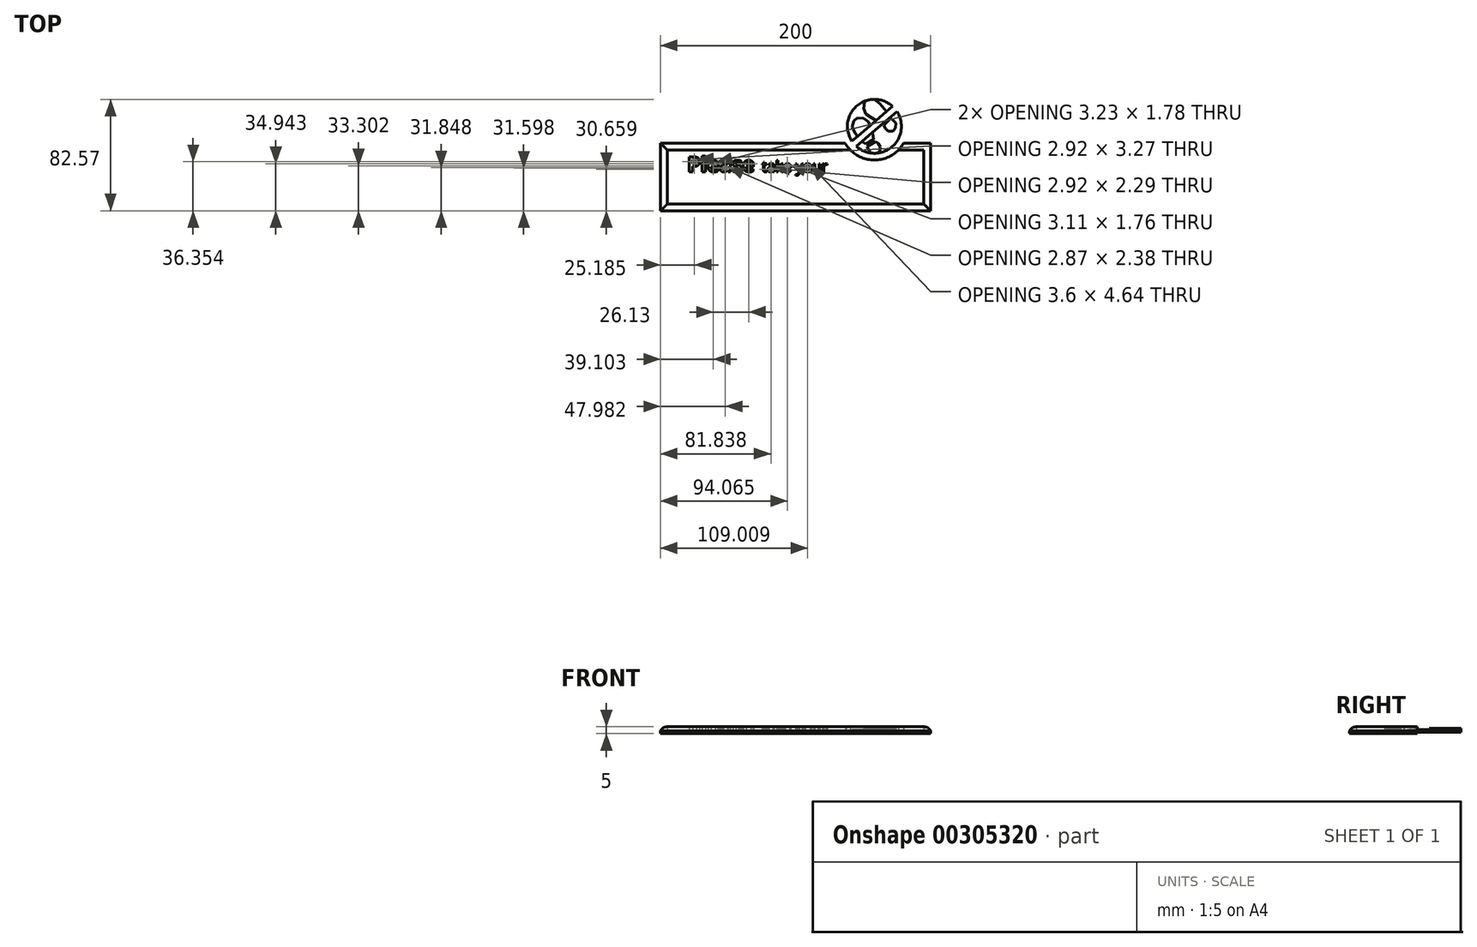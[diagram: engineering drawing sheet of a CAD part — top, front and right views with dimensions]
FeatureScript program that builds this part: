
annotation { "Feature Type Name" : "Feature", "Feature Type Description" : "" }
export const myFeature = defineFeature(function(context is Context, id is Id, definition is map)
    precondition{}
    {
        {
            var Q0;
            Q0=qCreatedBy(makeId("Top.planeOp"),FACE);
            var sketch = newSketch(context, id + "F0", { "sketchPlane" : qUnion([Q0])});
            skLineSegment(sketch, "E0.top", {"start": v(-121.35, -25.22) * mm, "end": v(78.65, -25.22) * mm});
            skLineSegment(sketch, "E0.left", {"start": v(-121.35, 24.78) * mm, "end": v(-121.35, -25.22) * mm});
            skLineSegment(sketch, "E0.right", {"start": v(78.65, 24.78) * mm, "end": v(78.65, -25.22) * mm});
            skCircle(sketch, "E1", {"center": v(37.04, 37.35) * mm, "radius": 25 * mm});
            skPoint(sketch, "E1.first.point", {"position": v(15.44, 24.78) * mm});
            skCircle(sketch, "E2", {"center": v(37.04, 37.35) * mm, "radius": 20 * mm});
            skLineSegment(sketch, "E3", {"start": v(20.32, 26.39) * mm, "end": v(50.53, 52.12) * mm});
            skLineSegment(sketch, "E4", {"start": v(53.77, 48.31) * mm, "end": v(23.56, 22.58) * mm});
            skLineSegment(sketch, "E5", {"start": v(20.32, 26.39) * mm, "end": v(23.56, 22.58) * mm, "construction": true});
            skLineSegment(sketch, "E6", {"start": v(21.94, 24.48) * mm, "end": v(52.27, 50.32) * mm, "construction": true});
            skPoint(sketch, "E7", {"position": v(58.65, 24.78) * mm});
            skLineSegment(sketch, "E8", {"start": v(-121.35, 24.78) * mm, "end": v(15.44, 24.78) * mm});
            skLineSegment(sketch, "E9", {"start": v(58.65, 24.78) * mm, "end": v(78.65, 24.78) * mm});
            skLineSegment(sketch, "E10", {"start": v(30.68, 24.1) * mm, "end": v(36.58, 27.82) * mm});
            skLineSegment(sketch, "E11", {"start": v(36.58, 27.82) * mm, "end": v(35.77, 32.31) * mm});
            skLineSegment(sketch, "E12", {"start": v(34.65, 36) * mm, "end": v(32.57, 40.8) * mm});
            skLineSegment(sketch, "E13", {"start": v(32.57, 40.8) * mm, "end": v(29.04, 43.21) * mm});
            skLineSegment(sketch, "E14", {"start": v(29.04, 43.21) * mm, "end": v(24.28, 43.73) * mm});
            skLineSegment(sketch, "E15", {"start": v(24.28, 43.73) * mm, "end": v(21.68, 41.4) * mm});
            skLineSegment(sketch, "E16", {"start": v(21.68, 41.4) * mm, "end": v(20.64, 36.9) * mm});
            skLineSegment(sketch, "E17", {"start": v(20.64, 36.9) * mm, "end": v(22.8, 32.31) * mm});
            skLineSegment(sketch, "E18", {"start": v(22.8, 32.31) * mm, "end": v(27.74, 26.17) * mm});
            skLineSegment(sketch, "E19", {"start": v(27.74, 26.17) * mm, "end": v(30.68, 24.1) * mm});
            skLineSegment(sketch, "E20", {"start": v(31.8, 22.28) * mm, "end": v(37.95, 26.17) * mm});
            skLineSegment(sketch, "E21", {"start": v(37.95, 26.17) * mm, "end": v(39.94, 24.61) * mm});
            skLineSegment(sketch, "E22", {"start": v(39.94, 24.61) * mm, "end": v(41.5, 22.02) * mm});
            skLineSegment(sketch, "E23", {"start": v(41.5, 22.02) * mm, "end": v(40.72, 18.47) * mm});
            skLineSegment(sketch, "E24", {"start": v(40.72, 18.47) * mm, "end": v(38.2, 17.09) * mm});
            skLineSegment(sketch, "E25", {"start": v(38.2, 17.09) * mm, "end": v(34.23, 17.78) * mm});
            skLineSegment(sketch, "E26", {"start": v(34.23, 17.78) * mm, "end": v(32.76, 20.03) * mm});
            skLineSegment(sketch, "E27", {"start": v(32.76, 20.03) * mm, "end": v(31.8, 22.28) * mm});
            skLineSegment(sketch, "E28", {"start": v(34.65, 36) * mm, "end": v(35.77, 32.31) * mm});
            skLineSegment(sketch, "E29", {"start": v(25.33, 53.56) * mm, "end": v(50.32, 22.39) * mm, "construction": true});
            skLineSegment(sketch, "E30.MirrorCS", {"start": v(29.21, 50.51) * mm, "end": v(29.74, 55.27) * mm});
            skLineSegment(sketch, "E31.MirrorCS", {"start": v(29.74, 55.27) * mm, "end": v(32.59, 57.3) * mm});
            skLineSegment(sketch, "E32.MirrorCS", {"start": v(32.59, 57.3) * mm, "end": v(37.2, 57.33) * mm});
            skLineSegment(sketch, "E33.MirrorCS", {"start": v(37.2, 57.33) * mm, "end": v(41.2, 54.22) * mm});
            skLineSegment(sketch, "E34.MirrorCS", {"start": v(41.2, 54.22) * mm, "end": v(46.13, 48.07) * mm});
            skLineSegment(sketch, "E35.MirrorCS", {"start": v(46.13, 48.07) * mm, "end": v(47.52, 44.75) * mm});
            skLineSegment(sketch, "E36.MirrorCS", {"start": v(47.52, 44.75) * mm, "end": v(42.6, 39.8) * mm});
            skLineSegment(sketch, "E37.MirrorCS", {"start": v(42.6, 39.8) * mm, "end": v(38.39, 41.56) * mm});
            skLineSegment(sketch, "E38.MirrorCS", {"start": v(35.03, 43.46) * mm, "end": v(38.39, 41.56) * mm});
            skLineSegment(sketch, "E39.MirrorCS", {"start": v(35.03, 43.46) * mm, "end": v(30.8, 46.54) * mm});
            skLineSegment(sketch, "E40.MirrorCS", {"start": v(30.8, 46.54) * mm, "end": v(29.21, 50.51) * mm});
            skLineSegment(sketch, "E41.MirrorCS", {"start": v(49.05, 43.26) * mm, "end": v(43.9, 38.1) * mm});
            skLineSegment(sketch, "E42.MirrorCS", {"start": v(43.9, 38.1) * mm, "end": v(45, 35.83) * mm});
            skLineSegment(sketch, "E43.MirrorCS", {"start": v(45, 35.83) * mm, "end": v(47.2, 33.74) * mm});
            skLineSegment(sketch, "E44.MirrorCS", {"start": v(47.2, 33.74) * mm, "end": v(50.82, 33.73) * mm});
            skLineSegment(sketch, "E45.MirrorCS", {"start": v(50.82, 33.73) * mm, "end": v(52.72, 35.88) * mm});
            skLineSegment(sketch, "E46.MirrorCS", {"start": v(52.72, 35.88) * mm, "end": v(52.9, 39.91) * mm});
            skLineSegment(sketch, "E47.MirrorCS", {"start": v(52.9, 39.91) * mm, "end": v(51.03, 41.84) * mm});
            skLineSegment(sketch, "E48.MirrorCS", {"start": v(51.03, 41.84) * mm, "end": v(49.05, 43.26) * mm});
            skText(sketch, "E49", { "text": "Please", "fontName": "OpenSans-Bold.ttf"});
            skText(sketch, "E50", { "text": "take your", "fontName": "OpenSans-Regular.ttf"});
            skText(sketch, "E51", { "text": "shoes off!", "fontName": "OpenSans-Bold.ttf"});
            skLineSegment(sketch, "E52.0", {"start": v(-116.35, 19.78) * mm, "end": v(19.27, 19.78) * mm});
            skLineSegment(sketch, "E52.1", {"start": v(54.82, 19.78) * mm, "end": v(73.65, 19.78) * mm});
            skLineSegment(sketch, "E52.2", {"start": v(73.65, 19.78) * mm, "end": v(73.65, -20.22) * mm});
            skLineSegment(sketch, "E52.3", {"start": v(-116.35, -20.22) * mm, "end": v(73.65, -20.22) * mm});
            skLineSegment(sketch, "E52.4", {"start": v(-116.35, 19.78) * mm, "end": v(-116.35, -20.22) * mm});
            skLineSegment(sketch, "E53", {"start": v(37.04, 37.35) * mm, "end": v(37.04, 62.35) * mm, "construction": true});
            const initialGuessF0  = {"E49": [-0.10135, 0.00366, 1, 0, 0.01112], "E50": [-0.04635, 0.00366, 1, 0, 0.008], "E51": [-0.03483, -0.01522, 1, 0, 0.014]};
            skSetInitialGuess(sketch, initialGuessF0);
            skSolve(sketch);
        }
        {
            var Q0;
            Q0=makeQuery(id+"F0.imprint","IMPRINT",FACE,{"disambiguationData":[TD([[makeQuery(id+"F0.imprint","IMPRINT",EDGE,{"derivedFrom":sQuery(id+"F0.wireOp",EDGE,"E0.top")}),1.0]])]});
            var Q1;
            Q1=makeQuery(id+"F0.imprint","IMPRINT",FACE,{"disambiguationData":[TD([[makeQuery(id+"F0.imprint","IMPRINT",EDGE,{"derivedFrom":sQuery(id+"F0.wireOp",EDGE,"E49.sketch_text.stroke-7")}),1.0]])]});
            var Q2;
            Q2=makeQuery(id+"F0.imprint","IMPRINT",FACE,{"disambiguationData":[TD([[makeQuery(id+"F0.imprint","IMPRINT",EDGE,{"derivedFrom":sQuery(id+"F0.wireOp",EDGE,"E49.sketch_text.stroke-0")}),1.0]])]});
            var Q3;
            Q3=makeQuery(id+"F0.imprint","IMPRINT",FACE,{"disambiguationData":[TD([[makeQuery(id+"F0.imprint","IMPRINT",EDGE,{"derivedFrom":sQuery(id+"F0.wireOp",EDGE,"E49.sketch_text.stroke-20")}),1.0]])]});
            var Q4;
            Q4=makeQuery(id+"F0.imprint","IMPRINT",FACE,{"disambiguationData":[TD([[makeQuery(id+"F0.imprint","IMPRINT",EDGE,{"derivedFrom":sQuery(id+"F0.wireOp",EDGE,"E49.sketch_text.stroke-58")}),1.0]])]});
            var Q5;
            Q5=makeQuery(id+"F0.imprint","IMPRINT",FACE,{"disambiguationData":[TD([[makeQuery(id+"F0.imprint","IMPRINT",EDGE,{"derivedFrom":sQuery(id+"F0.wireOp",EDGE,"E49.sketch_text.stroke-91")}),1.0]])]});
            var Q6;
            Q6=makeQuery(id+"F0.imprint","IMPRINT",FACE,{"disambiguationData":[TD([[makeQuery(id+"F0.imprint","IMPRINT",EDGE,{"derivedFrom":sQuery(id+"F0.wireOp",EDGE,"E50.sketch_text.stroke-38")}),1.0]])]});
            var Q7;
            Q7=makeQuery(id+"F0.imprint","IMPRINT",FACE,{"disambiguationData":[TD([[makeQuery(id+"F0.imprint","IMPRINT",EDGE,{"derivedFrom":sQuery(id+"F0.wireOp",EDGE,"E50.sketch_text.stroke-75")}),1.0]])]});
            var Q8;
            Q8=makeQuery(id+"F0.imprint","IMPRINT",FACE,{"disambiguationData":[TD([[makeQuery(id+"F0.imprint","IMPRINT",EDGE,{"derivedFrom":sQuery(id+"F0.wireOp",EDGE,"E50.sketch_text.stroke-105")}),1.0]])]});
            var Q9;
            Q9=makeQuery(id+"F0.imprint","IMPRINT",FACE,{"disambiguationData":[TD([[makeQuery(id+"F0.imprint","IMPRINT",EDGE,{"derivedFrom":sQuery(id+"F0.wireOp",EDGE,"E51.sketch_text.stroke-0")}),-1.0]])]});
            var Q10;
            Q10=makeQuery(id+"F0.imprint","IMPRINT",FACE,{"disambiguationData":[TD([[makeQuery(id+"F0.imprint","IMPRINT",EDGE,{"derivedFrom":sQuery(id+"F0.wireOp",EDGE,"E51.sketch_text.stroke-26")}),-1.0]])]});
            var Q11;
            Q11=makeQuery(id+"F0.imprint","IMPRINT",FACE,{"disambiguationData":[TD([[makeQuery(id+"F0.imprint","IMPRINT",EDGE,{"derivedFrom":sQuery(id+"F0.wireOp",EDGE,"E51.sketch_text.stroke-43")}),-1.0]])]});
            var Q12;
            Q12=makeQuery(id+"F0.imprint","IMPRINT",FACE,{"disambiguationData":[TD([[makeQuery(id+"F0.imprint","IMPRINT",EDGE,{"derivedFrom":sQuery(id+"F0.wireOp",EDGE,"E51.sketch_text.stroke-43")}),1.0]])]});
            var Q13;
            Q13=makeQuery(id+"F0.imprint","IMPRINT",FACE,{"disambiguationData":[TD([[makeQuery(id+"F0.imprint","IMPRINT",EDGE,{"derivedFrom":sQuery(id+"F0.wireOp",EDGE,"E51.sketch_text.stroke-61")}),1.0]])]});
            var Q14;
            Q14=makeQuery(id+"F0.imprint","IMPRINT",FACE,{"disambiguationData":[TD([[makeQuery(id+"F0.imprint","IMPRINT",EDGE,{"derivedFrom":sQuery(id+"F0.wireOp",EDGE,"E51.sketch_text.stroke-61")}),-1.0]])]});
            var Q15;
            Q15=makeQuery(id+"F0.imprint","IMPRINT",FACE,{"disambiguationData":[TD([[makeQuery(id+"F0.imprint","IMPRINT",EDGE,{"derivedFrom":sQuery(id+"F0.wireOp",EDGE,"E51.sketch_text.stroke-81")}),-1.0]])]});
            var Q16;
            Q16=makeQuery(id+"F0.imprint","IMPRINT",FACE,{"disambiguationData":[TD([[makeQuery(id+"F0.imprint","IMPRINT",EDGE,{"derivedFrom":sQuery(id+"F0.wireOp",EDGE,"E51.sketch_text.stroke-107")}),-1.0]])]});
            var Q17;
            Q17=makeQuery(id+"F0.imprint","IMPRINT",FACE,{"disambiguationData":[TD([[makeQuery(id+"F0.imprint","IMPRINT",EDGE,{"derivedFrom":sQuery(id+"F0.wireOp",EDGE,"E51.sketch_text.stroke-107")}),1.0]])]});
            var Q18;
            Q18=makeQuery(id+"F0.imprint","IMPRINT",FACE,{"disambiguationData":[TD([[makeQuery(id+"F0.imprint","IMPRINT",EDGE,{"derivedFrom":sQuery(id+"F0.wireOp",EDGE,"E51.sketch_text.stroke-143")}),-1.0]])]});
            var Q19;
            Q19=makeQuery(id+"F0.imprint","IMPRINT",FACE,{"disambiguationData":[TD([[makeQuery(id+"F0.imprint","IMPRINT",EDGE,{"derivedFrom":sQuery(id+"F0.wireOp",EDGE,"E51.sketch_text.stroke-161")}),-1.0]])]});
            var Q20;
            Q20=makeQuery(id+"F0.imprint","IMPRINT",FACE,{"disambiguationData":[TD([[makeQuery(id+"F0.imprint","IMPRINT",EDGE,{"derivedFrom":sQuery(id+"F0.wireOp",EDGE,"E51.sketch_text.stroke-165")}),-1.0]])]});
            var Q21;
            Q21=makeQuery(id+"F0.imprint","IMPRINT",FACE,{"disambiguationData":[TD([[makeQuery(id+"F0.imprint","IMPRINT",EDGE,{"derivedFrom":sQuery(id+"F0.wireOp",EDGE,"E51.sketch_text.stroke-125")}),-1.0]])]});
            var Q22;
            Q22=makeQuery(id+"F0.imprint","IMPRINT",FACE,{"disambiguationData":[TD([[makeQuery(id+"F0.imprint","IMPRINT",EDGE,{"derivedFrom":sQuery(id+"F0.wireOp",EDGE,"E49.sketch_text.stroke-0")}),-1.0]])]});
            var Q23;
            Q23=makeQuery(id+"F0.imprint","IMPRINT",FACE,{"disambiguationData":[TD([[makeQuery(id+"F0.imprint","IMPRINT",EDGE,{"derivedFrom":sQuery(id+"F0.wireOp",EDGE,"E49.sketch_text.stroke-16")}),-1.0]])]});
            var Q24;
            Q24=makeQuery(id+"F0.imprint","IMPRINT",FACE,{"disambiguationData":[TD([[makeQuery(id+"F0.imprint","IMPRINT",EDGE,{"derivedFrom":sQuery(id+"F0.wireOp",EDGE,"E49.sketch_text.stroke-20")}),-1.0]])]});
            var Q25;
            Q25=makeQuery(id+"F0.imprint","IMPRINT",FACE,{"disambiguationData":[TD([[makeQuery(id+"F0.imprint","IMPRINT",EDGE,{"derivedFrom":sQuery(id+"F0.wireOp",EDGE,"E49.sketch_text.stroke-40")}),-1.0]])]});
            var Q26;
            Q26=makeQuery(id+"F0.imprint","IMPRINT",FACE,{"disambiguationData":[TD([[makeQuery(id+"F0.imprint","IMPRINT",EDGE,{"derivedFrom":sQuery(id+"F0.wireOp",EDGE,"E49.sketch_text.stroke-65")}),-1.0]])]});
            var Q27;
            Q27=makeQuery(id+"F0.imprint","IMPRINT",FACE,{"disambiguationData":[TD([[makeQuery(id+"F0.imprint","IMPRINT",EDGE,{"derivedFrom":sQuery(id+"F0.wireOp",EDGE,"E49.sketch_text.stroke-91")}),-1.0]])]});
            var Q28;
            Q28=makeQuery(id+"F0.imprint","IMPRINT",FACE,{"disambiguationData":[TD([[makeQuery(id+"F0.imprint","IMPRINT",EDGE,{"derivedFrom":sQuery(id+"F0.wireOp",EDGE,"E50.sketch_text.stroke-0")}),-1.0]])]});
            var Q29;
            Q29=makeQuery(id+"F0.imprint","IMPRINT",FACE,{"disambiguationData":[TD([[makeQuery(id+"F0.imprint","IMPRINT",EDGE,{"derivedFrom":sQuery(id+"F0.wireOp",EDGE,"E50.sketch_text.stroke-19")}),-1.0]])]});
            var Q30;
            Q30=makeQuery(id+"F0.imprint","IMPRINT",FACE,{"disambiguationData":[TD([[makeQuery(id+"F0.imprint","IMPRINT",EDGE,{"derivedFrom":sQuery(id+"F0.wireOp",EDGE,"E50.sketch_text.stroke-46")}),-1.0]])]});
            var Q31;
            Q31=makeQuery(id+"F0.imprint","IMPRINT",FACE,{"disambiguationData":[TD([[makeQuery(id+"F0.imprint","IMPRINT",EDGE,{"derivedFrom":sQuery(id+"F0.wireOp",EDGE,"E50.sketch_text.stroke-61")}),-1.0]])]});
            var Q32;
            Q32=makeQuery(id+"F0.imprint","IMPRINT",FACE,{"disambiguationData":[TD([[makeQuery(id+"F0.imprint","IMPRINT",EDGE,{"derivedFrom":sQuery(id+"F0.wireOp",EDGE,"E50.sketch_text.stroke-80")}),-1.0]])]});
            var Q33;
            Q33=makeQuery(id+"F0.imprint","IMPRINT",FACE,{"disambiguationData":[TD([[makeQuery(id+"F0.imprint","IMPRINT",EDGE,{"derivedFrom":sQuery(id+"F0.wireOp",EDGE,"E50.sketch_text.stroke-96")}),-1.0]])]});
            var Q34;
            Q34=makeQuery(id+"F0.imprint","IMPRINT",FACE,{"disambiguationData":[TD([[makeQuery(id+"F0.imprint","IMPRINT",EDGE,{"derivedFrom":sQuery(id+"F0.wireOp",EDGE,"E50.sketch_text.stroke-113")}),-1.0]])]});
            var Q35;
            Q35=makeQuery(id+"F0.imprint","IMPRINT",FACE,{"disambiguationData":[TD([[makeQuery(id+"F0.imprint","IMPRINT",EDGE,{"derivedFrom":sQuery(id+"F0.wireOp",EDGE,"E50.sketch_text.stroke-130")}),-1.0]])]});
            extrude(context, id + "F1", {"entities" : qUnion([Q0, Q1, Q2, Q3, Q4, Q5, Q6, Q7, Q8, Q9, Q10, Q11, Q12, Q13, Q14, Q15, Q16, Q17, Q18, Q19, Q20, Q21, Q22, Q23, Q24, Q25, Q26, Q27, Q28, Q29, Q30, Q31, Q32, Q33, Q34, Q35]), "depth" : 2 * mm});
        }
        {
            var Q0;
            {var subQ8=sQuery(id+"F0.wireOp",EDGE,"E13");Q0=makeQuery(id+"F0.imprint","IMPRINT",FACE,{"disambiguationData":[TD([[makeQuery(id+"F0.imprint","IMPRINT",EDGE,{"derivedFrom":subQ8}),-1.0]])]});}
            var Q1;
            {var subQ0=sQuery(id+"F0.wireOp",EDGE,"E33.MirrorCS");Q1=makeQuery(id+"F0.imprint","IMPRINT",FACE,{"disambiguationData":[TD([[makeQuery(id+"F0.imprint","IMPRINT",EDGE,{"derivedFrom":subQ0}),1.0]])]});}
            var Q2;
            {var subQ12=sQuery(id+"F0.wireOp",EDGE,"E10");Q2=makeQuery(id+"F0.imprint","IMPRINT",FACE,{"disambiguationData":[TD([[makeQuery(id+"F0.imprint","IMPRINT",EDGE,{"derivedFrom":subQ12}),-1.0]])]});}
            extrude(context, id + "F2", {"entities" : qUnion([Q0, Q1, Q2]), "depth" : 2 * mm, "hasSecondDirection" : true, "secondDirectionOppositeDirection" : false, "secondDirectionDepth" : 1 * mm});
        }
        {
            var Q0;
            Q0=makeQuery(id+"F0.imprint","IMPRINT",FACE,{"disambiguationData":[TD([[makeQuery(id+"F0.imprint","IMPRINT",EDGE,{"derivedFrom":sQuery(id+"F0.wireOp",EDGE,"E0.top")}),1.0]])]});
            var Q1;
            Q1=makeQuery(id+"F0.imprint","IMPRINT",FACE,{"disambiguationData":[TD([[makeQuery(id+"F0.imprint","IMPRINT",EDGE,{"derivedFrom":sQuery(id+"F0.wireOp",EDGE,"E49.sketch_text.stroke-0")}),-1.0]])]});
            var Q2;
            Q2=makeQuery(id+"F0.imprint","IMPRINT",FACE,{"disambiguationData":[TD([[makeQuery(id+"F0.imprint","IMPRINT",EDGE,{"derivedFrom":sQuery(id+"F0.wireOp",EDGE,"E49.sketch_text.stroke-16")}),-1.0]])]});
            var Q3;
            Q3=makeQuery(id+"F0.imprint","IMPRINT",FACE,{"disambiguationData":[TD([[makeQuery(id+"F0.imprint","IMPRINT",EDGE,{"derivedFrom":sQuery(id+"F0.wireOp",EDGE,"E49.sketch_text.stroke-20")}),-1.0]])]});
            var Q4;
            Q4=makeQuery(id+"F0.imprint","IMPRINT",FACE,{"disambiguationData":[TD([[makeQuery(id+"F0.imprint","IMPRINT",EDGE,{"derivedFrom":sQuery(id+"F0.wireOp",EDGE,"E49.sketch_text.stroke-40")}),-1.0]])]});
            var Q5;
            Q5=makeQuery(id+"F0.imprint","IMPRINT",FACE,{"disambiguationData":[TD([[makeQuery(id+"F0.imprint","IMPRINT",EDGE,{"derivedFrom":sQuery(id+"F0.wireOp",EDGE,"E49.sketch_text.stroke-65")}),-1.0]])]});
            var Q6;
            Q6=makeQuery(id+"F0.imprint","IMPRINT",FACE,{"disambiguationData":[TD([[makeQuery(id+"F0.imprint","IMPRINT",EDGE,{"derivedFrom":sQuery(id+"F0.wireOp",EDGE,"E49.sketch_text.stroke-91")}),-1.0]])]});
            var Q7;
            Q7=makeQuery(id+"F0.imprint","IMPRINT",FACE,{"disambiguationData":[TD([[makeQuery(id+"F0.imprint","IMPRINT",EDGE,{"derivedFrom":sQuery(id+"F0.wireOp",EDGE,"E50.sketch_text.stroke-0")}),-1.0]])]});
            var Q8;
            Q8=makeQuery(id+"F0.imprint","IMPRINT",FACE,{"disambiguationData":[TD([[makeQuery(id+"F0.imprint","IMPRINT",EDGE,{"derivedFrom":sQuery(id+"F0.wireOp",EDGE,"E50.sketch_text.stroke-19")}),-1.0]])]});
            var Q9;
            Q9=makeQuery(id+"F0.imprint","IMPRINT",FACE,{"disambiguationData":[TD([[makeQuery(id+"F0.imprint","IMPRINT",EDGE,{"derivedFrom":sQuery(id+"F0.wireOp",EDGE,"E50.sketch_text.stroke-46")}),-1.0]])]});
            var Q10;
            Q10=makeQuery(id+"F0.imprint","IMPRINT",FACE,{"disambiguationData":[TD([[makeQuery(id+"F0.imprint","IMPRINT",EDGE,{"derivedFrom":sQuery(id+"F0.wireOp",EDGE,"E50.sketch_text.stroke-61")}),-1.0]])]});
            var Q11;
            Q11=makeQuery(id+"F0.imprint","IMPRINT",FACE,{"disambiguationData":[TD([[makeQuery(id+"F0.imprint","IMPRINT",EDGE,{"derivedFrom":sQuery(id+"F0.wireOp",EDGE,"E50.sketch_text.stroke-80")}),-1.0]])]});
            var Q12;
            Q12=makeQuery(id+"F0.imprint","IMPRINT",FACE,{"disambiguationData":[TD([[makeQuery(id+"F0.imprint","IMPRINT",EDGE,{"derivedFrom":sQuery(id+"F0.wireOp",EDGE,"E50.sketch_text.stroke-96")}),-1.0]])]});
            var Q13;
            Q13=makeQuery(id+"F0.imprint","IMPRINT",FACE,{"disambiguationData":[TD([[makeQuery(id+"F0.imprint","IMPRINT",EDGE,{"derivedFrom":sQuery(id+"F0.wireOp",EDGE,"E50.sketch_text.stroke-113")}),-1.0]])]});
            var Q14;
            Q14=makeQuery(id+"F0.imprint","IMPRINT",FACE,{"disambiguationData":[TD([[makeQuery(id+"F0.imprint","IMPRINT",EDGE,{"derivedFrom":sQuery(id+"F0.wireOp",EDGE,"E50.sketch_text.stroke-130")}),-1.0]])]});
            extrude(context, id + "F3", {"entities" : qUnion([Q0, Q1, Q2, Q3, Q4, Q5, Q6, Q7, Q8, Q9, Q10, Q11, Q12, Q13, Q14]), "depth" : 5 * mm, "hasSecondDirection" : true, "secondDirectionOppositeDirection" : false, "secondDirectionDepth" : 2 * mm});
        }
        {
            var Q0;
            {var subQ0=sQuery(id+"F0.wireOp",EDGE,"E13");Q0=makeQuery(id+"F0.imprint","IMPRINT",FACE,{"disambiguationData":[TD([[makeQuery(id+"F0.imprint","IMPRINT",EDGE,{"derivedFrom":subQ0}),1.0]])]});}
            var Q1;
            {var subQ1=sQuery(id+"F0.wireOp",EDGE,"E10");Q1=makeQuery(id+"F0.imprint","IMPRINT",FACE,{"disambiguationData":[TD([[makeQuery(id+"F0.imprint","IMPRINT",EDGE,{"derivedFrom":subQ1}),1.0]])]});}
            var Q2;
            Q2=makeQuery(id+"F0.imprint","IMPRINT",FACE,{"disambiguationData":[TD([[makeQuery(id+"F0.imprint","IMPRINT",EDGE,{"derivedFrom":sQuery(id+"F0.wireOp",EDGE,"E20")}),-1.0]])]});
            extrude(context, id + "F4", {"entities" : qUnion([Q0, Q1, Q2]), "operationType" : NewBodyOperationType.ADD, "depth" : 3 * mm, "hasSecondDirection" : true, "secondDirectionOppositeDirection" : false, "secondDirectionDepth" : 1 * mm});
        }
        {
            var Q0;
            {var subQ1=sQuery(id+"F0.wireOp",EDGE,"E30.MirrorCS");Q0=makeQuery(id+"F0.imprint","IMPRINT",FACE,{"disambiguationData":[TD([[makeQuery(id+"F0.imprint","IMPRINT",EDGE,{"derivedFrom":subQ1}),-1.0]])]});}
            var Q1;
            Q1=makeQuery(id+"F0.imprint","IMPRINT",FACE,{"disambiguationData":[TD([[makeQuery(id+"F0.imprint","IMPRINT",EDGE,{"derivedFrom":sQuery(id+"F0.wireOp",EDGE,"E41.MirrorCS")}),1.0]])]});
            extrude(context, id + "F5", {"entities" : qUnion([Q0, Q1]), "operationType" : NewBodyOperationType.ADD, "depth" : 4 * mm, "hasSecondDirection" : true, "secondDirectionOppositeDirection" : false, "secondDirectionDepth" : 1 * mm});
        }
        {
            var Q0;
            Q0=makeQuery(id+"F3.opExtrude","CAP_EDGE",EDGE,{"disambiguationData":[OSD([sQuery(id+"F0.wireOp",EDGE,"E0.left")])],"isStart":false});
            var Q1;
            Q1=makeQuery(id+"F3.opExtrude","CAP_EDGE",EDGE,{"disambiguationData":[OSD([sQuery(id+"F0.wireOp",EDGE,"E0.top")])],"isStart":false});
            var Q2;
            Q2=makeQuery(id+"F3.opExtrude","CAP_EDGE",EDGE,{"disambiguationData":[OSD([sQuery(id+"F0.wireOp",EDGE,"E8")])],"isStart":false});
            var Q3;
            Q3=makeQuery(id+"F3.opExtrude","CAP_EDGE",EDGE,{"disambiguationData":[OSD([sQuery(id+"F0.wireOp",EDGE,"E0.right")])],"isStart":false});
            fillet(context, id + "F6", {"entities" : qUnion([Q0, Q1, Q2, Q3]), "radius" : 5 * mm, "tangentPropagation" : true, "allowEdgeOverflow" : false});
        }
    });
